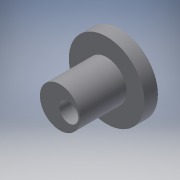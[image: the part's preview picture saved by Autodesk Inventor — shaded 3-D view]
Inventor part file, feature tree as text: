
AUTODESK INVENTOR PART (.ipt)
format: ipt  version: 2016 (Build 200138000, 138)  size: 111,616 bytes
history: native  units: in
note: dims shown in document units (in); Inventor stores cm internally (conversion verified against a paired STEP export)
features: extrude x3, reference x2, sketch x2
ambient origin geometry x8: Origin, YZ Plane, XZ Plane, XY Plane, X Axis, Y Axis, Z Axis, Center Point
bodies: Solid1 (feature_tree)
feature tree (7):
  extrude  "Extrusion1"  Depth=0.4134in TaperAngle=0.0deg
  extrude  "Extrusion2"  Depth=0.1181in
  extrude  "Extrusion3"  Depth=0.1969in TaperAngle=0.0deg
  reference  "Reference1"
  sketch  "Sketch2"  dims[d0=0.5512in d1=0.4134in d2=0.0in]
  sketch  "Sketch3"  dims[d3=0.0984in d4=0.1673in d5=0.1969in d6=0.0in d7=0.4724in d8=0.1181in d9=0.0in]
  reference  "Reference2"
